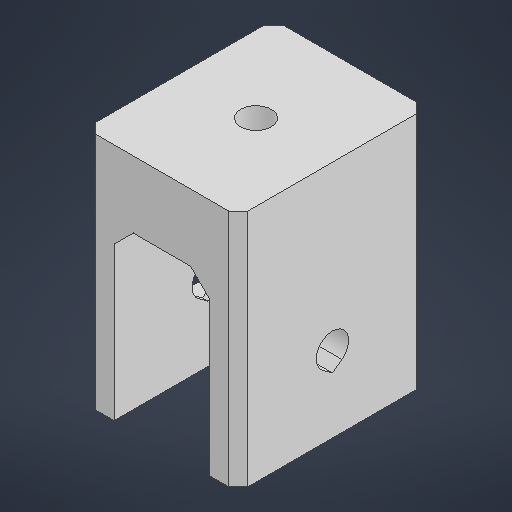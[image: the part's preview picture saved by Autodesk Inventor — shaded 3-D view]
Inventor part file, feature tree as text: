
AUTODESK INVENTOR PART (.ipt)
format: ipt  version: 2025.1 (Build 291241000, 241)  size: 510,464 bytes
history: native  units: mm
features: extrude x6, sketch x4, chamfer x2, projected_geometry x1
ambient origin geometry x8: Origin, YZ Plane, XZ Plane, XY Plane, X Axis, Y Axis, Z Axis, Center Point
bodies: Body1 (feature_tree)
feature tree (13):
  sketch  "Sketch3"  dims[d12=19.7mm d13=25.0mm d14=0.0mm]
  extrude  "Extrusion3"  Depth=25.0mm TaperAngle=0.0deg
  sketch  "Sketch4"  dims[d15=3.4mm d16=8.0mm]
  extrude  "Extrusion4"  Depth=8.0mm
  extrude  "Extrusion5"  TaperAngle=0.0deg  [1 undecoded]
  sketch  "Sketch7"  dims[d18=18.0mm d19=0.0mm d20=0.0mm d21=0.0mm]
  extrude  "Extrusion8"  Depth=2.4mm TaperAngle=0.0deg
  extrude  "Extrusion9"  Depth=10.0mm
  chamfer  "Chamfer2"  Distance=7.2mm
  chamfer  "Chamfer3"  Distance=3.0mm
  extrude  "Extrusion10"  Depth=16.0mm
  projected_geometry  "Projected Loop1"
  sketch  "Sketch9"  dims[d30=3.2mm d31=5.5mm d32=0.0mm d36=10.0mm d41=5.0mm d42=0.0mm d44=2.0mm d45=2.0mm d46=45.0deg d47=7.2mm d48=3.0mm d49=0.0mm d52=16.0mm d53=2.1mm d54=1.0mm d55=2.0mm d56=45.0deg d57=5.6mm d58=5.7mm d59=2.4mm d60=0.0mm d51=0.5mm]
note: 1 required parameter value undecoded (feature->parameter linkage not recoverable at this tier; creation-order binding heuristic only, values carry confidence <= 0.55)
